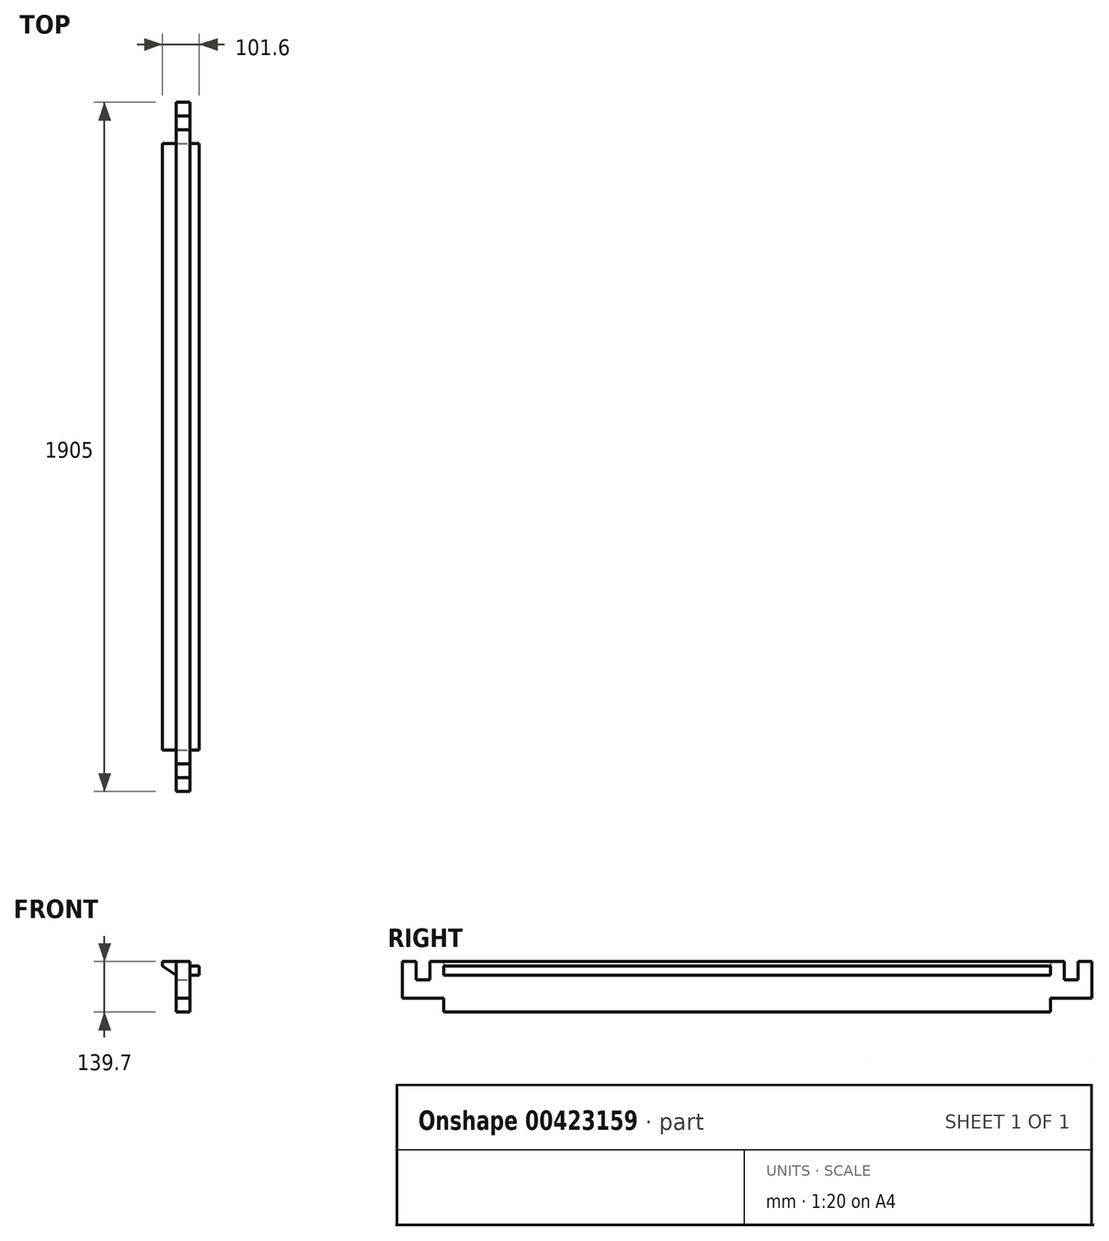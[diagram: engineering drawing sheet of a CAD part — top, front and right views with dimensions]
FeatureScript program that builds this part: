
annotation { "Feature Type Name" : "Feature", "Feature Type Description" : "" }
export const myFeature = defineFeature(function(context is Context, id is Id, definition is map)
    precondition{}
    {
        {
            var Q0;
            Q0=qCreatedBy(makeId("Top.planeOp"),FACE);
            var sketch = newSketch(context, id + "F0", { "sketchPlane" : qUnion([Q0])});
            skLineSegment(sketch, "E0.bottom", {"start": v(-19.05, 0) * mm, "end": v(19.05, 0) * mm});
            skLineSegment(sketch, "E0.top", {"start": v(-19.05, 952.5) * mm, "end": v(19.05, 952.5) * mm});
            skLineSegment(sketch, "E0.left", {"start": v(-19.05, 0) * mm, "end": v(-19.05, 952.5) * mm});
            skLineSegment(sketch, "E0.right", {"start": v(19.05, 0) * mm, "end": v(19.05, 952.5) * mm});
            skSolve(sketch);
        }
        {
            var Q0;
            Q0=makeQuery(id+"F0.imprint","IMPRINT",FACE,{"disambiguationData":[TD([[makeQuery(id+"F0.imprint","IMPRINT",EDGE,{"derivedFrom":sQuery(id+"F0.wireOp",EDGE,"E0.bottom")}),1.0]])]});
            extrude(context, id + "F1", {"entities" : qUnion([Q0]), "oppositeDirection" : true, "depth" : 139.7 * mm});
        }
        {
            var Q0;
            Q0=makeQuery(id+"F1.opExtrude","SWEPT_FACE",FACE,{"disambiguationData":[OSD([sQuery(id+"F0.wireOp",EDGE,"E0.right")])]});
            var sketch = newSketch(context, id + "F2", { "sketchPlane" : qUnion([Q0])});
            skLineSegment(sketch, "E1.bottom", {"start": v(0, -139.7) * mm, "end": v(114.3, -139.7) * mm});
            skLineSegment(sketch, "E1.top", {"start": v(0, -101.6) * mm, "end": v(114.3, -101.6) * mm});
            skLineSegment(sketch, "E1.left", {"start": v(0, -139.7) * mm, "end": v(0, -101.6) * mm});
            skLineSegment(sketch, "E1.right", {"start": v(114.3, -139.7) * mm, "end": v(114.3, -101.6) * mm});
            skSolve(sketch);
        }
        {
            var Q0;
            Q0=makeQuery(id+"F2.imprint","IMPRINT",FACE,{"disambiguationData":[TD([[makeQuery(id+"F2.imprint","IMPRINT",EDGE,{"derivedFrom":sQuery(id+"F2.wireOp",EDGE,"E1.bottom")}),1.0]])]});
            extrude(context, id + "F3", {"entities" : qUnion([Q0]), "operationType" : NewBodyOperationType.REMOVE, "endBound" : BoundingType.THROUGH_ALL, "oppositeDirection" : true, "depth" : 25.4 * mm});
        }
        {
            var Q0;
            Q0=makeQuery(id+"F1.opExtrude","SWEPT_FACE",FACE,{"disambiguationData":[OSD([sQuery(id+"F0.wireOp",EDGE,"E0.right")])]});
            var sketch = newSketch(context, id + "F4", { "sketchPlane" : qUnion([Q0])});
            skLineSegment(sketch, "E2.top", {"start": v(38.1, -50.8) * mm, "end": v(76.2, -50.8) * mm});
            skLineSegment(sketch, "E3", {"start": v(57.15, -50.8) * mm, "end": v(57.15, -101.6) * mm, "construction": true});
            skLineSegment(sketch, "E4", {"start": v(38.1, -50.8) * mm, "end": v(0, -50.8) * mm, "construction": true});
            skLineSegment(sketch, "E5", {"start": v(38.1, -50.8) * mm, "end": v(38.1, 0) * mm});
            skLineSegment(sketch, "E6", {"start": v(38.1, 0) * mm, "end": v(76.2, 0) * mm});
            skLineSegment(sketch, "E7", {"start": v(76.2, 0) * mm, "end": v(76.2, -50.8) * mm});
            skSolve(sketch);
        }
        {
            var Q0;
            Q0=makeQuery(id+"F4.imprint","IMPRINT",FACE,{"disambiguationData":[TD([[makeQuery(id+"F4.imprint","IMPRINT",EDGE,{"derivedFrom":sQuery(id+"F4.wireOp",EDGE,"E2.top")}),1.0]])]});
            extrude(context, id + "F5", {"entities" : qUnion([Q0]), "operationType" : NewBodyOperationType.REMOVE, "endBound" : BoundingType.THROUGH_ALL, "oppositeDirection" : true, "depth" : 25.4 * mm});
        }
        {
            var Q0;
            Q0=makeQuery(id+"F1.opExtrude","SWEPT_FACE",FACE,{"disambiguationData":[OSD([sQuery(id+"F0.wireOp",EDGE,"E0.top")])]});
            cPlane(context, id + "F6", {"entities" : qUnion([Q0]), "cplaneType" : CPlaneType.OFFSET, "offset" : 0 * mm, "width" : 152.4 * mm, "height" : 152.4 * mm});
        }
        {
            var Q0;
            Q0=makeQuery(id+"F1.opExtrude","SWEPT_BODY",BODY,{"disambiguationData":[OSD([sQuery(id+"F0.wireOp",EDGE,"E0.bottom"),sQuery(id+"F0.wireOp",EDGE,"E0.top"),sQuery(id+"F0.wireOp",EDGE,"E0.left"),sQuery(id+"F0.wireOp",EDGE,"E0.right")])]});
            var Q1;
            Q1=qCreatedBy(id+"F6.planeOp",FACE);
            mirror(context, id + "F7", {"operationType" : NewBodyOperationType.ADD, "entities" : qUnion([Q0]), "mirrorPlane" : qUnion([Q1])});
        }
        {
            var Q0;
            Q0=qCreatedBy(id+"F6.planeOp",FACE);
            var sketch = newSketch(context, id + "F8", { "sketchPlane" : qUnion([Q0])});
            skLineSegment(sketch, "E8", {"start": v(57.15, 0) * mm, "end": v(19.05, 0) * mm});
            skLineSegment(sketch, "E9", {"start": v(19.05, 0) * mm, "end": v(19.05, -38.1) * mm});
            skLineSegment(sketch, "E10", {"start": v(57.15, 0) * mm, "end": v(57.15, -12.7) * mm});
            skLineSegment(sketch, "E11", {"start": v(57.15, -12.7) * mm, "end": v(19.05, -38.1) * mm});
            skSolve(sketch);
        }
        {
            var Q0;
            Q0=makeQuery(id+"F8.imprint","IMPRINT",FACE,{"disambiguationData":[TD([[makeQuery(id+"F8.imprint","IMPRINT",EDGE,{"derivedFrom":sQuery(id+"F8.wireOp",EDGE,"E8")}),1.0]])]});
            extrude(context, id + "F9", {"entities" : qUnion([Q0]), "depth" : 838.2 * mm, "hasSecondDirection" : true, "secondDirectionOppositeDirection" : true, "secondDirectionDepth" : 838.2 * mm});
        }
        {
            var Q0;
            Q0=qCreatedBy(id+"F6.planeOp",FACE);
            var sketch = newSketch(context, id + "F10", { "sketchPlane" : qUnion([Q0])});
            skLineSegment(sketch, "E12.bottom", {"start": v(-19.05, -12.7) * mm, "end": v(-44.45, -12.7) * mm});
            skLineSegment(sketch, "E12.top", {"start": v(-19.05, -38.1) * mm, "end": v(-44.45, -38.1) * mm});
            skLineSegment(sketch, "E12.left", {"start": v(-19.05, -12.7) * mm, "end": v(-19.05, -38.1) * mm});
            skLineSegment(sketch, "E12.right", {"start": v(-44.45, -12.7) * mm, "end": v(-44.45, -38.1) * mm});
            skSolve(sketch);
        }
        {
            var Q0;
            Q0=makeQuery(id+"F10.imprint","IMPRINT",FACE,{"disambiguationData":[TD([[makeQuery(id+"F10.imprint","IMPRINT",EDGE,{"derivedFrom":sQuery(id+"F10.wireOp",EDGE,"E12.bottom")}),1.0]])]});
            extrude(context, id + "F11", {"entities" : qUnion([Q0]), "depth" : 838.2 * mm, "hasSecondDirection" : true, "secondDirectionOppositeDirection" : true, "secondDirectionDepth" : 838.2 * mm});
        }
    });
